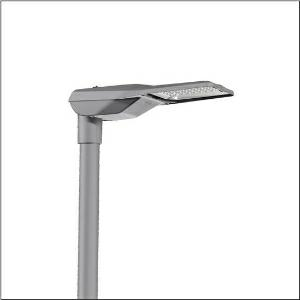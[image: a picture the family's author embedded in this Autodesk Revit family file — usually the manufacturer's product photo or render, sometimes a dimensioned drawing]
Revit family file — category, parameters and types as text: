
# Revit family: streetlight_sl_21_mini___st1_5a_5xe2p43s08hb_a927
name_source: partatom
category: Lighting Fixtures
units: mm (PartAtom-declared; Revit-internal decimal feet)

## family parameters
Cut with Voids When Loaded = No
Host = Face
Light Source = No
Part Type = Normal
Room Calculation Point = No
Round Connector Dimension = Use Diameter
Shared = No

## types (1)
- --- (1 x LED, 9260 lm, 66 W, 4000K)
    Apparent Load = 66 VA
    CIE Flux Codes = 22 53 95 100 100
    Color Rendering = 70
    Color Temperature = 4000K
    Default Elevation = 1800 mm
    Description = Streetlight SL 21 mini, mast luminaire, primary light control with lens, of PMMA, primary optical cover: cover, of toughened safety glass, transparent, light distribution: ST1.5a, light emission: direct distribution, primary light characteristic: asymmetric, installation type: side-entry, post-top, LED, High Power LED, rated luminous flux: 9.260lm, luminous efficacy: 140lm/W, light colour: 740, colour temperature: 4000K, control gear: D4i, control: overheat protection, constant luminous flux control, time-dependent luminous flux control, flexible luminous flux parameterisation, pre-setting: logarithmic dimming characteristic, mains connection: 220..240V, AC, 50/60Hz, start of lifetime: 66W, end of service life: 69W, reduction: 30W, luminaire housing, of diecast aluminium, powder-coated, SITECO metallic grey (DB 702S), corrosivity category C5 high according to DIN EN ISO 12944, please order mast flange separately, inclination adjustable: 0°, 5°, 10°, 15°, sealing non-destructively replaceable, multi-level sealing system, length: 628mm, width: 235mm, height: 110mm, mast flange for spigot size: 42mm (side-entry): 5XC10008XM4, 60/48mm (side-entry/post-top): 5XC10108XM2, 76/60mm (side-entry/post-top): 5XC10108XM1, mounting height: 4..8m, Smart Interface above, protection rating (complete): IP66, insulation class (complete): insulation class II (safety insulation), certification: CE, ENEC, ENEC+, VDE, impact resistance: IK10, permissible operating ambient temperature for outdoor applications: -40..+50°C, standard-compliant lighting for roads and squares, packaging unit: 1 piece

Light Distribution: ST1.5a
    Height = 110 mm
    Lamp = 1 x LED
    Lamp Light Flux = 9260 lm
    Lamp Power = 66 W
    Lamp count = 1
    Length = 625 mm
    Luminous efficacy = 140 lm/W
    Manufacturer = Siteco
    ModVariant = No
    Model = 5XE2P43S08HB
    Number of Poles = 1
    OnlyDefault = Yes
    Power Factor = 1
    Product Name = Streetlight SL 21 mini | ST1.5a
    Product group = mast luminaire | pylon top
    ProductGroupID = 6100
    Protection Class = Protection class II
    Protection Degree = IP 66
    RLX_Detail_Level = 1
    RLX_Emergency_Light_Flux = 0 lm
    RLX_Emergency_Type = 0
    RLX_Emergency_Type_DB = No
    RlxData = <blob elided: 29609 chars, md5=91e35912>
    Socket = socket
    Standby Power = 0 W
    System Light Flux = 9260 lm
    System Power = 66 W
    Type Comments = factory setting: luminous flux: 100 % | dim-lin: 254 | 670 mA
    Type Image = l_1003515.jpg
    URL = http://relux.com
    VarID = @adj_175089
    Voltage = 0 V
    Weight = 0.00 kg
    Width = 234 mm

## geometry (parser evidence)
native form markers: Blend x4, Sweep x10
no freeform markers — native parametric forms only
